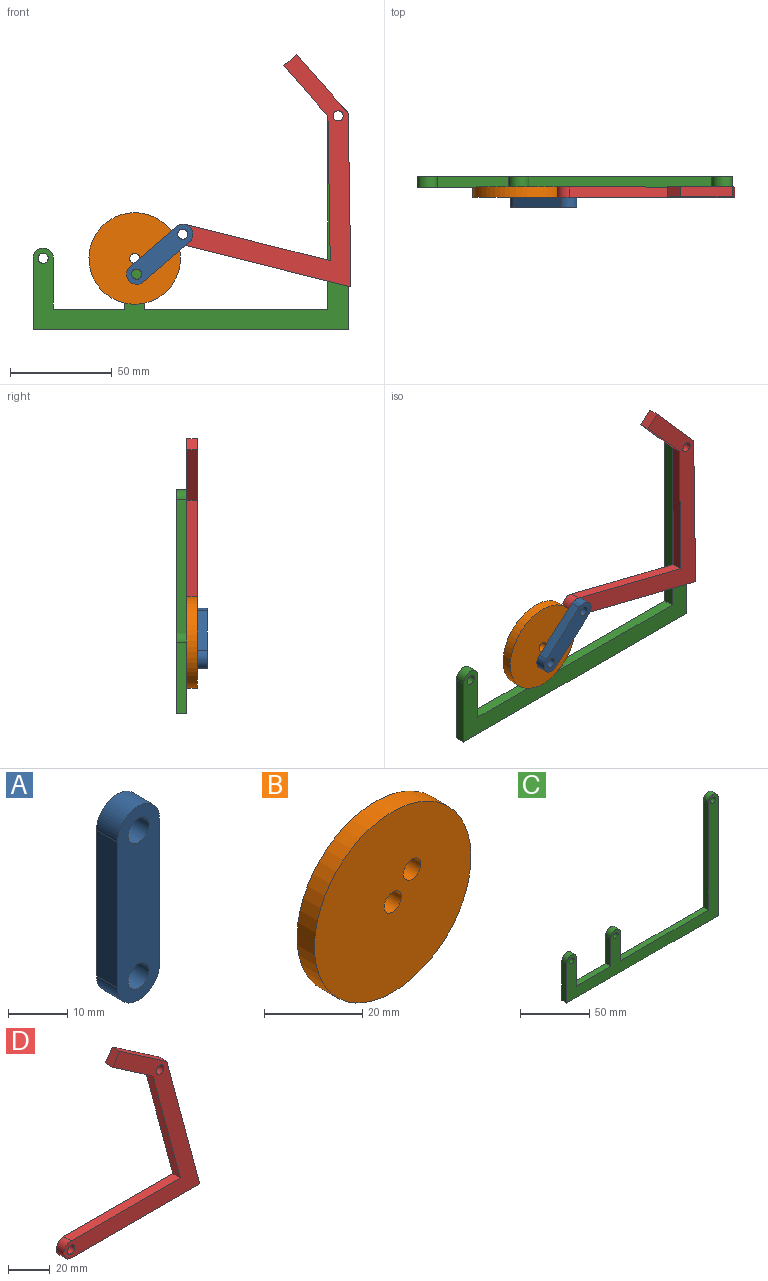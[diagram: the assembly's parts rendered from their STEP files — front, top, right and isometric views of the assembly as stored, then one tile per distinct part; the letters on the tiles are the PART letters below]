
ASSEMBLY  parts=4 mates=4
PART A: 8 faces, bbox 10x5x40 mm
  f0: plane 30x5mm, normal (1,0,0), area 150mm2, adj f1,f5,f6,f7
  f1: cylinder r=5mm len=10mm, axis (0,1,0), area 78.5mm2, adj f0,f2,f6,f7
  f2: plane 30x5mm, normal (-1,0,0), area 150mm2, adj f1,f5,f6,f7
  f3: cylinder r=2.5mm len=5mm, axis (0,1,0), area 78.5mm2, adj f6,f7
  f4: cylinder r=2.5mm len=5mm, axis (0,1,0), area 78.5mm2, adj f6,f7
  f5: cylinder r=5mm len=10mm, axis (0,1,0), area 78.5mm2, adj f0,f2,f6,f7
  f6: plane 40x10mm, normal (0,-1,0), area 339.3mm2, adj f0,f1,f2,f3,f4,f5
  f7: plane 40x10mm, normal (0,1,0), area 339.3mm2, adj f0,f1,f2,f3,f4,f5
PART B: 5 faces, bbox 45x5x45 mm
  f0: cylinder r=2.5mm len=5mm, axis (0,1,0), area 78.5mm2, adj f3,f4
  f1: cylinder r=2.5mm len=5mm, axis (0,1,0), area 78.5mm2, adj f3,f4
  f2: cylinder r=22.5mm len=45mm, axis (0,1,0), area 706.9mm2, adj f3,f4
  f3: plane 45x45mm, normal (0,-1,0), area 1551.2mm2, adj f0,f1,f2
  f4: plane 45x45mm, normal (0,1,0), area 1551.2mm2, adj f0,f1,f2
PART C: 17 faces, bbox 155x5x110 mm
  f0: plane 105x5mm, normal (1,0,0), area 525mm2, adj f1,f13,f15,f16
  f1: cylinder r=5mm len=10mm, axis (0,1,0), area 78.5mm2, adj f0,f2,f15,f16
  f2: plane 95x5mm, normal (-1,0,0), area 475mm2, adj f1,f3,f15,f16
  f3: plane 90x5mm, normal (0,0,1), area 450mm2, adj f2,f4,f15,f16
  f4: plane 25x5mm, normal (1,0,0), area 125mm2, adj f3,f5,f15,f16
  f5: cylinder r=5mm len=10mm, axis (0,1,0), area 78.5mm2, adj f4,f6,f15,f16
  f6: plane 25x5mm, normal (-1,0,0), area 125mm2, adj f5,f7,f15,f16
  f7: plane 35x5mm, normal (0,0,1), area 175mm2, adj f6,f8,f15,f16
  f8: plane 25x5mm, normal (1,0,0), area 125mm2, adj f7,f9,f15,f16
  f9: cylinder r=5mm len=10mm, axis (0,1,0), area 78.5mm2, adj f8,f10,f15,f16
  f10: plane 35x5mm, normal (-1,0,0), area 175mm2, adj f9,f13,f15,f16
  f11: cylinder r=2.5mm len=5mm, axis (0,1,0), area 78.5mm2, adj f15,f16
  f12: cylinder r=2.5mm len=5mm, axis (0,1,0), area 78.5mm2, adj f15,f16
  f13: plane 155x5mm, normal (0,0,-1), area 775mm2, adj f0,f10,f15,f16
  f14: cylinder r=2.5mm len=5mm, axis (0,1,0), area 78.5mm2, adj f15,f16
  f15: plane 155x110mm, normal (0,-1,0), area 3058.9mm2, adj f0,f1,f2,f3,f4,f5,f6,f7
  f16: plane 155x110mm, normal (0,1,0), area 3058.9mm2, adj f0,f1,f2,f3,f4,f5,f6,f7
PART D: 12 faces, bbox 91.5x5x104.3 mm
  f0: plane 73.48x5mm, normal (0,0,1), area 367.4mm2, adj f1,f9,f10,f11
  f1: cylinder r=5mm len=10mm, axis (0,1,0), area 78.5mm2, adj f0,f2,f10,f11
  f2: plane 86.52x5mm, normal (0,0,-1), area 432.6mm2, adj f1,f3,f10,f11
  f3: plane 82.5x22.1mm, normal (0.97,0,0.26), area 427mm2, adj f2,f4,f10,f11
  f4: plane 31.69x21.77mm, normal (0.57,0,0.82), area 192.2mm2, adj f3,f5,f10,f11
  f5: plane 6.93x5mm, normal (-0.82,0,0.57), area 42.1mm2, adj f4,f6,f10,f11
  f6: plane 27.11x18.62mm, normal (-0.57,0,-0.82), area 164.5mm2, adj f5,f9,f10,f11
  f7: cylinder r=2.5mm len=5mm, axis (0,1,0), area 78.5mm2, adj f10,f11
  f8: cylinder r=2.5mm len=5mm, axis (0,1,0), area 78.5mm2, adj f10,f11
  f9: plane 68.71x18.41mm, normal (-0.97,0,-0.26), area 355.6mm2, adj f0,f6,f10,f11
  f10: plane 104.26x91.52mm, normal (0,-1,0), area 1882.7mm2, adj f0,f1,f2,f3,f4,f5,f6,f7
  f11: plane 104.26x91.52mm, normal (0,1,0), area 1882.7mm2, adj f0,f1,f2,f3,f4,f5,f6,f7
PLACE A rot(axis=(0,-1,0),130.9deg) t=(-54.09,-18.64,3.75)mm
PLACE B rot(axis=(0,1,0),127.1deg) t=(-77.72,-13.64,-8.18)mm
PLACE C t=(-36.8,-8.64,10.52)mm fixed
PLACE D rot(axis=(0,1,0),14.1deg) t=(23.51,-13.64,-15.72)mm
MATE revolute D.f7 <-> C.f1  axis (0,1,0) through (22.27,-13.64,61.92)mm
MATE revolute A.f1 <-> B.f1  axis (0,1,0) through (-76.77,-18.64,-15.89)mm
MATE revolute A.f4 <-> D.f1  axis (0,1,0) through (-54.09,-18.64,3.75)mm
MATE revolute B.f4 <-> C.f5  axis (0,1,0) through (-77.73,-13.64,-8.08)mm
